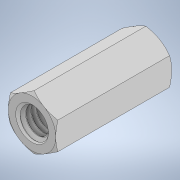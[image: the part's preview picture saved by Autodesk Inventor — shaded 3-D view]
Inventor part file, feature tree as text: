
AUTODESK INVENTOR PART (.ipt)
format: ipt  version: 2020 (Build 240168000, 168)  size: 636,416 bytes
history: native  units: in
note: dims shown in document units (in); Inventor stores cm internally (conversion verified against a paired STEP export)
features: mirror x1
ambient origin geometry x8: Origin, YZ Plane, XZ Plane, XY Plane, X Axis, Y Axis, Z Axis, Center Point
bodies: Solid1 (feature_tree)
feature tree (1):
  mirror  "Mirror1"
